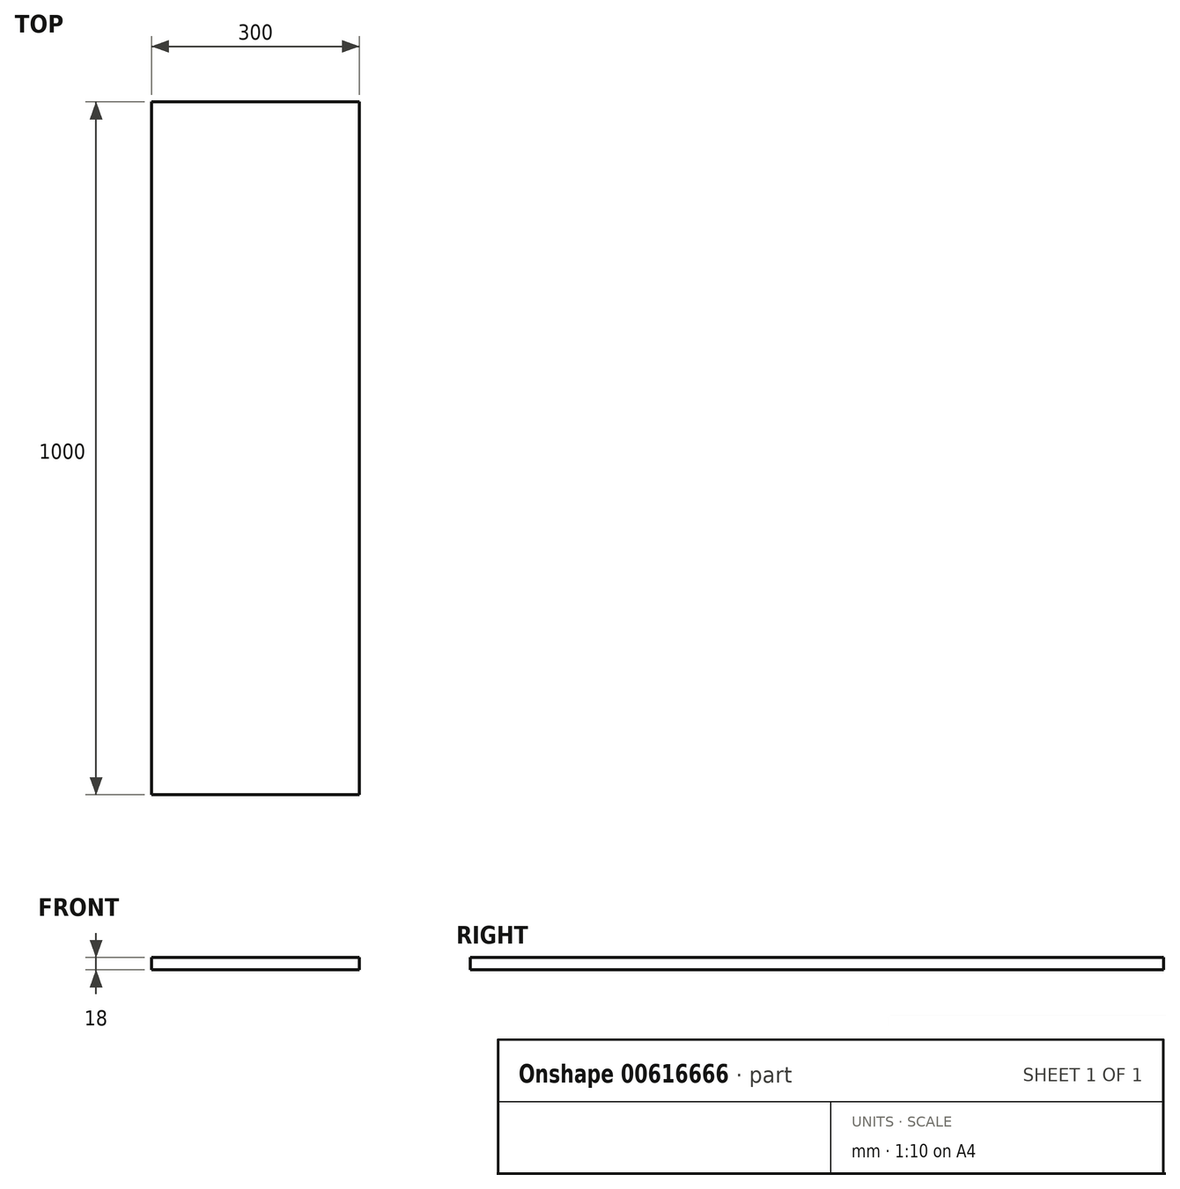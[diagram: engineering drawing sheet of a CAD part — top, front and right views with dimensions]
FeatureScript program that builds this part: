
annotation { "Feature Type Name" : "Feature", "Feature Type Description" : "" }
export const myFeature = defineFeature(function(context is Context, id is Id, definition is map)
    precondition{}
    {
        {
            var Q0;
            Q0=qCreatedBy(makeId("Top.planeOp"),FACE);
            var sketch = newSketch(context, id + "F0", { "sketchPlane" : qUnion([Q0])});
            skLineSegment(sketch, "E0.bottom", {"start": v(0, 0) * mm, "end": v(300, 0) * mm});
            skLineSegment(sketch, "E0.top", {"start": v(0, 1000) * mm, "end": v(300, 1000) * mm});
            skLineSegment(sketch, "E0.left", {"start": v(0, 0) * mm, "end": v(0, 1000) * mm});
            skLineSegment(sketch, "E0.right", {"start": v(300, 0) * mm, "end": v(300, 1000) * mm});
            skSolve(sketch);
        }
        {
            var Q0;
            Q0=makeQuery(id+"F0.imprint","IMPRINT",FACE,{"disambiguationData":[TD([[makeQuery(id+"F0.imprint","IMPRINT",EDGE,{"derivedFrom":sQuery(id+"F0.wireOp",EDGE,"E0.bottom")}),1.0]])]});
            extrude(context, id + "F1", {"entities" : qUnion([Q0]), "depth" : 18 * mm, "offsetDistance" : 25 * mm});
        }
    });
